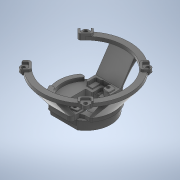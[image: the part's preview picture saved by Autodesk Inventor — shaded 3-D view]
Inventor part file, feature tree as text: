
AUTODESK INVENTOR PART (.ipt)
format: ipt  version: 2020 (Build 240168000, 168)  size: 1,460,736 bytes
history: native  units: mm
features: projected_geometry x52, sketch x31, extrude x24, other x9, fillet x9, chamfer x4, loft x2, revolve x1, pattern_circular x1, mirror x1
ambient origin geometry x8: Origin, YZ Plane, XZ Plane, XY Plane, X Axis, Y Axis, Z Axis, Center Point
bodies: Body1 (feature_tree)
feature tree (134):
  other  "Твердое тело1"
  extrude  "Выдавливание1"  Depth=17.1mm
  extrude  "Выдавливание2"  Depth=17.1mm
  other  "РабПлоскость1"
  sketch  "Эскиз3"
  other  "РабОсь1"
  revolve  "Вращение1"
  extrude  "Выдавливание3"  Depth=25.0mm
  extrude  "Выдавливание4"  Depth=5.3mm
  extrude  "Выдавливание5"  Depth=44.7mm
  extrude  "Выдавливание6"  Depth=7.7mm TaperAngle=0.0deg
  extrude  "Выдавливание7"  Depth=5.0mm
  extrude  "Выдавливание8"  Depth=30.65mm
  sketch  "Эскиз10"
  extrude  "Выдавливание9"  Depth=2.5mm TaperAngle=0.0deg
  fillet  "Сопряжение1"  Radius=0.2mm
  fillet  "Сопряжение2"  [1 undecoded]
  fillet  "Сопряжение3"  Radius=1.85mm
  extrude  "Выдавливание10"  Depth=30.0mm
  fillet  "Сопряжение4"  Radius=2.0mm
  fillet  "Сопряжение5"  Radius=3.0mm
  extrude  "камера"  Depth=38.0mm
  extrude  "труба"  Depth=10.0mm TaperAngle=0.0deg
  sketch  "Эскиз15"
  other  "РабПлоскость2"
  extrude  "Выдавливание12"  Depth=5.2mm
  extrude  "Выдавливание13"  Depth=6.2mm
  chamfer  "Фаска1"  Distance=29.46mm
  fillet  "Сопряжение6"  Radius=10.0mm
  fillet  "Сопряжение7"  Radius=9.5mm
  other  "РабОсь2"
  pattern_circular  "Круговой массив1"  [2 undecoded]
  extrude  "Выдавливание15"  TaperAngle=60.0deg  [1 undecoded]
  chamfer  "Фаска2"  Distance=6.0mm
  sketch  "Эскиз20"
  extrude  "Выдавливание16"  Depth=6.0mm
  fillet  "Сопряжение8"  Radius=14.2mm
  other  "РабПлоскость3"
  extrude  "Выдавливание17"  Depth=9.5mm
  extrude  "Выдавливание18"  Depth=2.0mm
  sketch  "Эскиз24"
  sketch  "Эскиз25"
  sketch  "Эскиз26"
  extrude  "Выдавливание19"  Depth=13.962634mm
  loft  "Лофт1"
  other  "РабПлоскость4"
  mirror  "Зеркальное отражение1"
  extrude  "Выдавливание20"  Depth=2.0mm TaperAngle=0.0deg
  loft  "Лофт2"
  extrude  "Выдавливание21"  Depth=6.2mm
  chamfer  "Фаска3"  Distance=6.0mm
  chamfer  "Фаска4"  Distance=1.7mm
  extrude  "Выдавливание22"  Depth=1.5mm TaperAngle=0.0deg
  extrude  "Выдавливание23"  Depth=6.0mm TaperAngle=0.0deg
  fillet  "Сопряжение9"  Radius=0.5mm
  extrude  "Выдавливание24"  Depth=0.7mm
  sketch  "Эскиз1"
  sketch  "Эскиз2"
  projected_geometry  "Спроецированная петля1"
  projected_geometry  "Спроецированная петля2"
  sketch  "Эскиз4"
  projected_geometry  "Спроецированная петля3"
  sketch  "Эскиз5"
  sketch  "Эскиз6"
  projected_geometry  "Спроецированная петля4"
  sketch  "Эскиз7"
  projected_geometry  "Спроецированная петля5"
  sketch  "Эскиз8"
  projected_geometry  "Спроецированная петля6"
  projected_geometry  "Спроецированная петля7"
  projected_geometry  "Спроецированная петля8"
  sketch  "Эскиз9"
  projected_geometry  "Спроецированная петля9"
  projected_geometry  "Спроецированная петля10"
  projected_geometry  "Спроецированная петля11"
  projected_geometry  "Спроецированная петля12"
  sketch  "Эскиз11"
  sketch  "Эскиз12"
  projected_geometry  "Спроецированная петля13"
  projected_geometry  "Спроецированная петля14"
  projected_geometry  "Спроецированная петля15"
  sketch  "Эскиз14"
  projected_geometry  "Спроецированная петля20"
  projected_geometry  "Спроецированная петля21"
  projected_geometry  "Спроецированная петля22"
  projected_geometry  "Спроецированная петля23"
  sketch  "Эскиз16"
  projected_geometry  "Спроецированная петля24"
  sketch  "Эскиз17"
  projected_geometry  "Спроецированная петля25"
  sketch  "Эскиз18"
  sketch  "Эскиз19"
  projected_geometry  "Спроецированная петля26"
  projected_geometry  "Спроецированная петля27"
  projected_geometry  "Спроецированная петля28"
  projected_geometry  "Спроецированная петля29"
  sketch  "Эскиз21"
  projected_geometry  "Спроецированная петля30"
  projected_geometry  "Спроецированная петля31"
  projected_geometry  "Спроецированная петля32"
  projected_geometry  "Спроецированная петля33"
  projected_geometry  "Спроецированная петля34"
  projected_geometry  "Спроецированная петля35"
  projected_geometry  "Спроецированная петля36"
  projected_geometry  "Спроецированная петля37"
  projected_geometry  "Спроецированная петля38"
  projected_geometry  "Спроецированная петля39"
  sketch  "Эскиз22"
  projected_geometry  "Спроецированная петля40"
  projected_geometry  "Спроецированная петля41"
  projected_geometry  "Спроецированная петля42"
  projected_geometry  "Спроецированная петля43"
  projected_geometry  "Спроецированная петля44"
  sketch  "Эскиз23"
  projected_geometry  "Спроецированная петля45"
  projected_geometry  "Спроецированная петля46"
  projected_geometry  "Спроецированная петля47"
  projected_geometry  "Спроецированная петля48"
  projected_geometry  "Спроецированная петля49"
  projected_geometry  "Спроецированная петля50"
  other  "Ребра1"
  sketch  "Эскиз27"
  projected_geometry  "Спроецированная петля51"
  sketch  "Эскиз28"
  projected_geometry  "Спроецированная петля52"
  projected_geometry  "Спроецированная петля53"
  other  "Ребра2"
  sketch  "Эскиз31"
  sketch  "Эскиз32"
  projected_geometry  "Спроецированная петля54"
  projected_geometry  "Спроецированная петля55"
  sketch  "Эскиз33"
  projected_geometry  "Спроецированная петля56"
  sketch  "Эскиз34"
note: 4 required parameter values undecoded (feature->parameter linkage not recoverable at this tier; creation-order binding heuristic only, values carry confidence <= 0.55)
